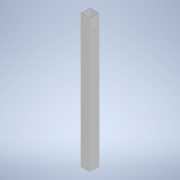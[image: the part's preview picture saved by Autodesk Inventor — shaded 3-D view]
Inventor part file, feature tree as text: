
AUTODESK INVENTOR PART (.ipt)
format: ipt  version: 2020.3 (Build 243373000, 373)  size: 126,464 bytes
history: native  units: mm
features: sketch x3, hole x2, other x1, extrude x1
ambient origin geometry x8: Origin, YZ Plane, XZ Plane, XY Plane, X Axis, Y Axis, Z Axis, Center Point
bodies: Body1 (feature_tree)
feature tree (7):
  other  "ソリッド1"
  extrude  "押し出し1"  Depth=15.0mm
  hole  "穴1"  [1 undecoded]
  hole  "穴2"  [1 undecoded]
  sketch  "スケッチ1"
  sketch  "スケッチ2"
  sketch  "スケッチ3"
note: 2 required parameter values undecoded (feature->parameter linkage not recoverable at this tier; creation-order binding heuristic only, values carry confidence <= 0.55)
